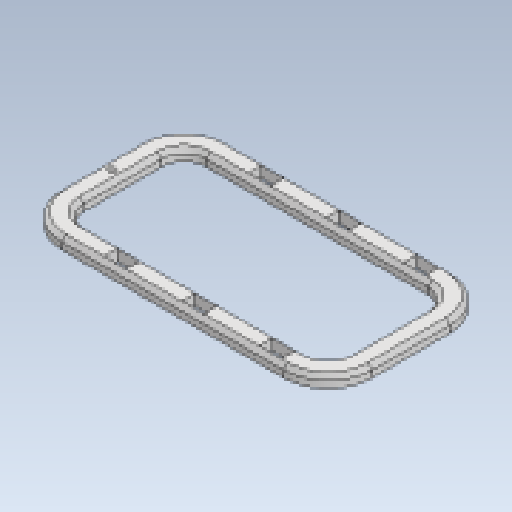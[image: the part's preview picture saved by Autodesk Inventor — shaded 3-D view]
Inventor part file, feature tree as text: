
AUTODESK INVENTOR PART (.ipt)
format: ipt  version: 2023 (Build 270158030, 158C)  size: 205,824 bytes
history: native  units: mm
features: other x4, sketch x2, sweep x1
ambient origin geometry x8: Origin, YZ Plane, XZ Plane, XY Plane, X Axis, Y Axis, Z Axis, Center Point
bodies: Body1 (feature_tree)
feature tree (7):
  other  "trebuchet-complete-parts.ipt"
  sweep  "Sweep1"
  other  "baseplate::trebuchet-complete-parts.ipt"
  other  "TaggingFeature1"
  sketch  "Sketch1"  dims[d0=10.0mm d1=2.5mm]
  sketch  "Sketch2"  dims[d2=1.0mm d3=37.5mm d4=37.5mm d5=0.174533mm d6=0.0mm]
  other  "baseplate"
